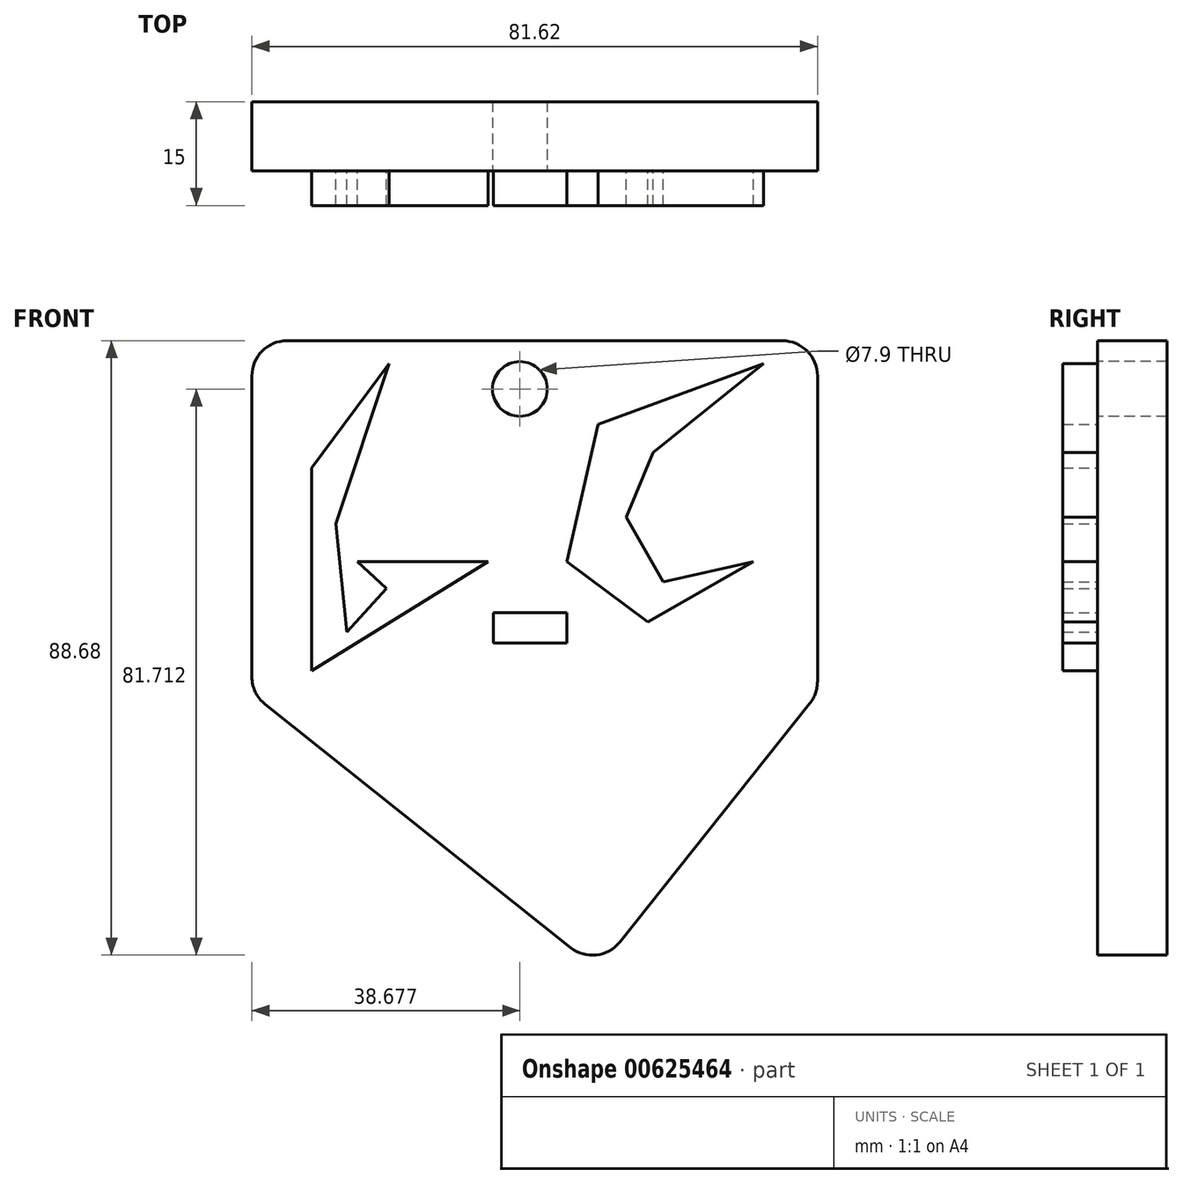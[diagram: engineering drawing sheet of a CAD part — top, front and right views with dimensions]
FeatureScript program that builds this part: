
annotation { "Feature Type Name" : "Feature", "Feature Type Description" : "" }
export const myFeature = defineFeature(function(context is Context, id is Id, definition is map)
    precondition{}
    {
        {
            var Q0;
            Q0=qCreatedBy(makeId("Front.planeOp"),FACE);
            var sketch = newSketch(context, id + "F0", { "sketchPlane" : qUnion([Q0])});
            skLineSegment(sketch, "E0", {"start": v(-49.95, 50.96) * mm, "end": v(-49.95, 0) * mm});
            skLineSegment(sketch, "E1", {"start": v(-49.95, 0) * mm, "end": v(0, -39.78) * mm});
            skLineSegment(sketch, "E2", {"start": v(0, -39.78) * mm, "end": v(31.67, 0) * mm});
            skLineSegment(sketch, "E3", {"start": v(31.67, 0) * mm, "end": v(31.67, 50.96) * mm});
            skLineSegment(sketch, "E4", {"start": v(31.67, 50.96) * mm, "end": v(-49.95, 50.96) * mm});
            skSolve(sketch);
        }
        {
            var Q0;
            Q0 = qSketchRegion(id + "F0", true);
            extrude(context, id + "F1", {"entities" : qUnion([Q0]), "depth" : 10 * mm, "offsetDistance" : 25.4 * mm});
        }
        {
            var Q0;
            Q0=makeQuery(id+"F1.opExtrude","CAP_FACE",FACE,{"disambiguationData":[OSD([sQuery(id+"F0.wireOp",EDGE,"E0"),sQuery(id+"F0.wireOp",EDGE,"E1"),sQuery(id+"F0.wireOp",EDGE,"E2"),sQuery(id+"F0.wireOp",EDGE,"E3"),sQuery(id+"F0.wireOp",EDGE,"E4")])],"isStart":false});
            var sketch = newSketch(context, id + "F2", { "sketchPlane" : qUnion([Q0])});
            skLineSegment(sketch, "E5", {"start": v(-30.15, 47.66) * mm, "end": v(-41.33, 32.63) * mm});
            skLineSegment(sketch, "E6", {"start": v(-41.33, 32.63) * mm, "end": v(-41.33, 3.3) * mm});
            skLineSegment(sketch, "E7", {"start": v(-41.33, 3.3) * mm, "end": v(-15.86, 19.06) * mm});
            skLineSegment(sketch, "E8", {"start": v(-15.86, 19.06) * mm, "end": v(-34.74, 19.06) * mm});
            skLineSegment(sketch, "E9", {"start": v(-34.74, 19.06) * mm, "end": v(-30.52, 15.21) * mm});
            skLineSegment(sketch, "E10", {"start": v(-30.52, 15.21) * mm, "end": v(-36.26, 8.93) * mm});
            skLineSegment(sketch, "E11", {"start": v(-36.26, 8.93) * mm, "end": v(-37.85, 24.56) * mm});
            skLineSegment(sketch, "E12", {"start": v(-37.85, 24.56) * mm, "end": v(-30.15, 47.66) * mm});
            skLineSegment(sketch, "E13", {"start": v(23.92, 47.66) * mm, "end": v(0, 38.86) * mm});
            skLineSegment(sketch, "E14", {"start": v(0, 38.86) * mm, "end": v(-4.5, 19.06) * mm});
            skLineSegment(sketch, "E15", {"start": v(-4.5, 19.06) * mm, "end": v(7.18, 10.38) * mm});
            skLineSegment(sketch, "E16", {"start": v(7.18, 10.38) * mm, "end": v(22.45, 19.06) * mm});
            skLineSegment(sketch, "E17", {"start": v(22.45, 19.06) * mm, "end": v(9.44, 16.13) * mm});
            skLineSegment(sketch, "E18", {"start": v(9.44, 16.13) * mm, "end": v(4.1, 25.52) * mm});
            skLineSegment(sketch, "E19", {"start": v(4.1, 25.52) * mm, "end": v(7.97, 34.83) * mm});
            skLineSegment(sketch, "E20", {"start": v(7.97, 34.83) * mm, "end": v(23.92, 47.66) * mm});
            skLineSegment(sketch, "E21", {"start": v(-15.12, 11.73) * mm, "end": v(-15.12, 7.33) * mm});
            skLineSegment(sketch, "E22", {"start": v(-15.12, 7.33) * mm, "end": v(-4.5, 7.33) * mm});
            skLineSegment(sketch, "E23", {"start": v(-4.5, 7.33) * mm, "end": v(-4.5, 11.73) * mm});
            skLineSegment(sketch, "E24", {"start": v(-4.5, 11.73) * mm, "end": v(-15.12, 11.73) * mm});
            skSolve(sketch);
        }
        {
            var Q0;
            Q0 = qSketchRegion(id + "F2", true);
            extrude(context, id + "F3", {"entities" : qUnion([Q0]), "operationType" : NewBodyOperationType.ADD, "depth" : 5 * mm, "offsetDistance" : 25.4 * mm});
        }
        {
            var Q0;
            Q0=makeQuery(id+"F1.opExtrude","CAP_FACE",FACE,{"disambiguationData":[OSD([sQuery(id+"F0.wireOp",EDGE,"E0"),sQuery(id+"F0.wireOp",EDGE,"E1"),sQuery(id+"F0.wireOp",EDGE,"E2"),sQuery(id+"F0.wireOp",EDGE,"E3"),sQuery(id+"F0.wireOp",EDGE,"E4")])],"isStart":false});
            var sketch = newSketch(context, id + "F4", { "sketchPlane" : qUnion([Q0])});
            skCircle(sketch, "E25", {"center": v(-11.27, 44) * mm, "radius": 3.95 * mm});
            skSolve(sketch);
        }
        {
            var Q0;
            Q0=makeQuery(id+"F4.imprint","IMPRINT",FACE,{"disambiguationData":[TD([[makeQuery(id+"F4.imprint","IMPRINT",EDGE,{"derivedFrom":sQuery(id+"F4.wireOp",EDGE,"E25")}),1.0]])]});
            extrude(context, id + "F5", {"entities" : qUnion([Q0]), "operationType" : NewBodyOperationType.REMOVE, "oppositeDirection" : true, "depth" : 101.1 * mm, "offsetDistance" : 25.4 * mm});
        }
        {
            var Q0;
            Q0=makeQuery(id+"F1.opExtrude","SWEPT_EDGE",EDGE,{"disambiguationData":[OSD([sQuery(id+"F0.wireOp",EDGE,"E0"),sQuery(id+"F0.wireOp",EDGE,"E4")])]});
            var Q1;
            Q1=makeQuery(id+"F1.opExtrude","SWEPT_EDGE",EDGE,{"disambiguationData":[OSD([sQuery(id+"F0.wireOp",EDGE,"E3"),sQuery(id+"F0.wireOp",EDGE,"E4")])]});
            var Q2;
            Q2=makeQuery(id+"F1.opExtrude","SWEPT_EDGE",EDGE,{"disambiguationData":[OSD([sQuery(id+"F0.wireOp",EDGE,"E2"),sQuery(id+"F0.wireOp",EDGE,"E3")])]});
            var Q3;
            Q3=makeQuery(id+"F1.opExtrude","SWEPT_EDGE",EDGE,{"disambiguationData":[OSD([sQuery(id+"F0.wireOp",EDGE,"E1"),sQuery(id+"F0.wireOp",EDGE,"E2")])]});
            var Q4;
            Q4=makeQuery(id+"F1.opExtrude","SWEPT_EDGE",EDGE,{"disambiguationData":[OSD([sQuery(id+"F0.wireOp",EDGE,"E0"),sQuery(id+"F0.wireOp",EDGE,"E1")])]});
            fillet(context, id + "F6", {"entities" : qUnion([Q0, Q1, Q2, Q3, Q4]), "radius" : 5.08 * mm, "tangentPropagation" : true, "allowEdgeOverflow" : false});
        }
    });
